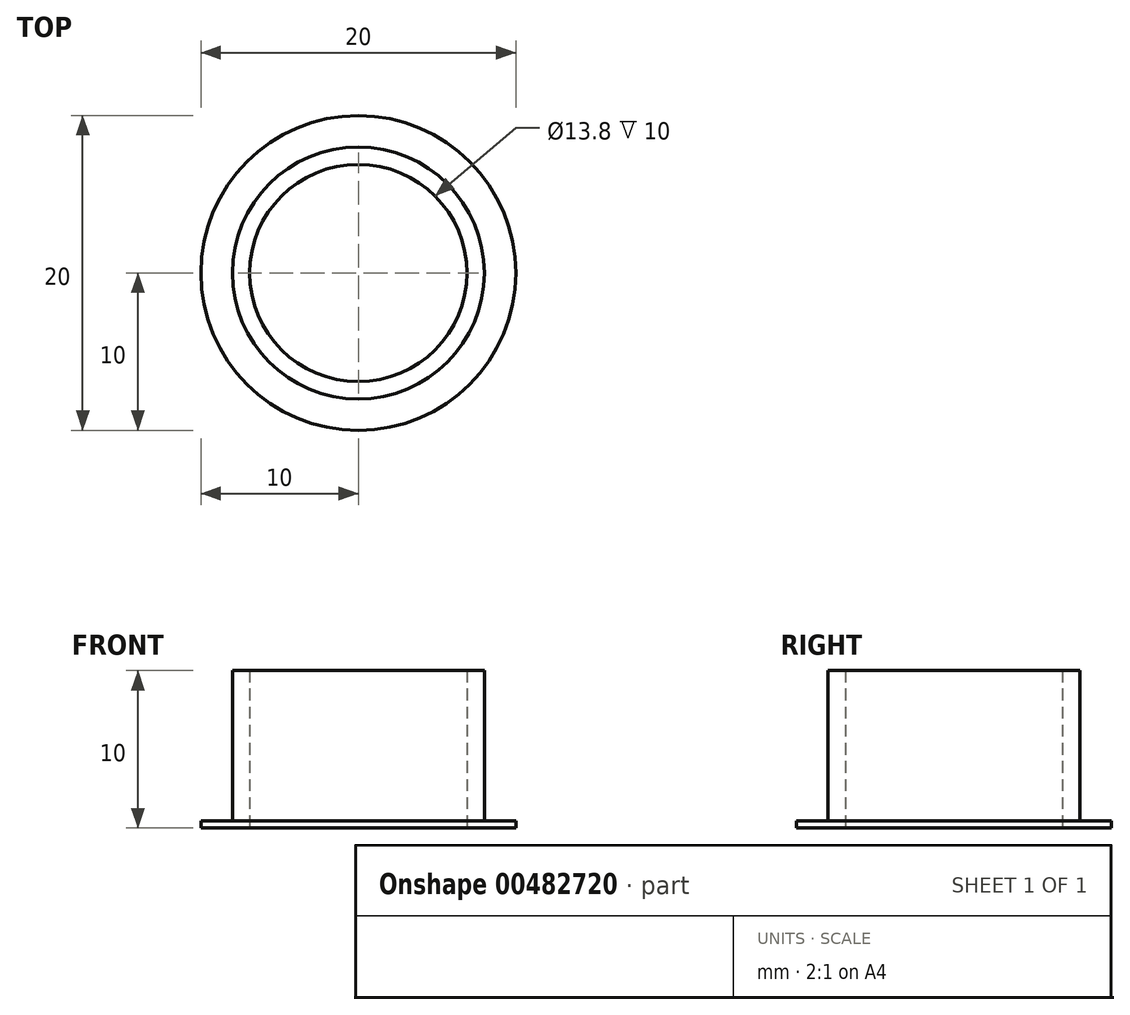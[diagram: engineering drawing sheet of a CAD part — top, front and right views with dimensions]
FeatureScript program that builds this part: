
annotation { "Feature Type Name" : "Feature", "Feature Type Description" : "" }
export const myFeature = defineFeature(function(context is Context, id is Id, definition is map)
    precondition{}
    {
        {
            assignVariable(context, id + "F0", {"name" : "H", "anyValue" : 10});
        }
        {
            var Q0;
            Q0=qCreatedBy(makeId("Top.planeOp"),FACE);
            var sketch = newSketch(context, id + "F1", { "sketchPlane" : qUnion([Q0])});
            skCircle(sketch, "E0", {"center": v(0, 0) * mm, "radius": 10 * mm});
            skCircle(sketch, "E1", {"center": v(0, 0) * mm, "radius": 8 * mm});
            skCircle(sketch, "E2", {"center": v(0, 0) * mm, "radius": 6.9 * mm});
            skSolve(sketch);
        }
        {
            assignVariable(context, id + "F2", {"name" : "H2", "anyValue" : 0.45});
        }
        {
            var Q0;
            Q0=makeQuery(id+"F1.imprint","IMPRINT",FACE,{"disambiguationData":[TD([[makeQuery(id+"F1.imprint","IMPRINT",EDGE,{"derivedFrom":sQuery(id+"F1.wireOp",EDGE,"E0")}),1.0]])]});
            extrude(context, id + "F3", {"entities" : qUnion([Q0]), "depth" : getVariable(context, 'H2') * mm});
        }
        {
            var Q0;
            Q0=makeQuery(id+"F1.imprint","IMPRINT",FACE,{"disambiguationData":[TD([[makeQuery(id+"F1.imprint","IMPRINT",EDGE,{"derivedFrom":sQuery(id+"F1.wireOp",EDGE,"E1")}),1.0]])]});
            extrude(context, id + "F4", {"entities" : qUnion([Q0]), "operationType" : NewBodyOperationType.ADD, "depth" : getVariable(context, 'H') * mm});
        }
    });
